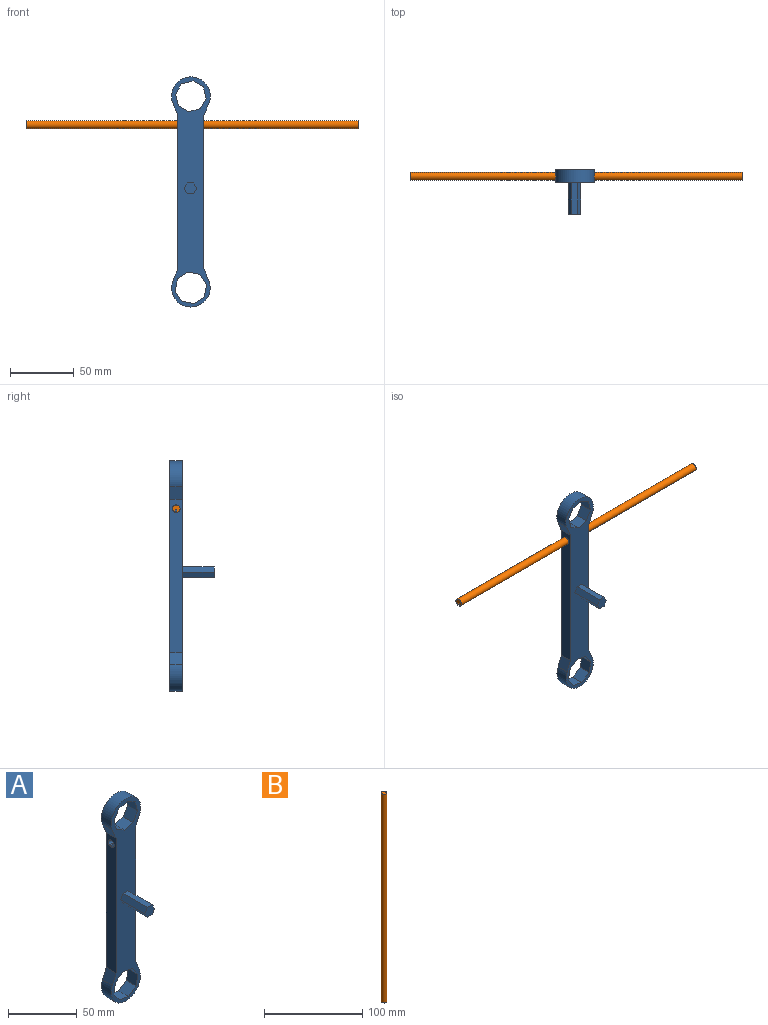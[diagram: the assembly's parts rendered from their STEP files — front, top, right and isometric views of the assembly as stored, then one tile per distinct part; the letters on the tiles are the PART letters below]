
ASSEMBLY  parts=2 mates=1
PART A: 37 faces, bbox 30.4x35x180.3 mm
  f0: plane 120x10mm, normal (1,0,0), area 1174.4mm2, adj f4,f5,f24,f25,f33,f34,f35,f36
  f1: plane 120x10mm, normal (-1,0,0), area 1174.4mm2, adj f2,f7,f24,f25,f33,f34,f35,f36
  f2: plane 10x9.24mm, normal (-0.92,0,0.38), area 100mm2, adj f1,f3,f24,f25
  f3: cylinder r=15.08mm len=30.16mm, axis (0,1,0), area 591.8mm2, adj f2,f4,f24,f25
  f4: plane 10x9.24mm, normal (0.92,0,0.38), area 100mm2, adj f0,f3,f24,f25
  f5: plane 10x10mm, normal (0.92,0,-0.39), area 108.5mm2, adj f0,f6,f24,f25
  f6: cylinder r=15.18mm len=30.36mm, axis (0,1,0), area 578.8mm2, adj f5,f7,f24,f25
  f7: plane 10x10mm, normal (-0.92,0,-0.39), area 108.5mm2, adj f1,f6,f24,f25
  f8: plane 10x8.02mm, normal (-0.51,0,-0.86), area 93mm2, adj f9,f22,f24,f25
  f9: plane 10x9mm, normal (-0.97,0,-0.25), area 93mm2, adj f8,f10,f24,f25
  f10: plane 10x8.02mm, normal (-0.86,0,0.51), area 93mm2, adj f9,f11,f24,f25
  f11: plane 10x9mm, normal (-0.25,0,0.97), area 93mm2, adj f10,f12,f24,f25
  f12: plane 10x8.02mm, normal (0.51,0,0.86), area 93mm2, adj f11,f13,f24,f25
  f13: plane 10x9mm, normal (0.97,0,0.25), area 93mm2, adj f12,f14,f24,f25
  f14: plane 10x8.02mm, normal (0.86,0,-0.51), area 93mm2, adj f13,f22,f24,f25
  f15: plane 10x7.99mm, normal (0.83,0,0.56), area 96.6mm2, adj f16,f23,f24,f25
  f16: plane 10x9.49mm, normal (0.98,0,-0.19), area 96.6mm2, adj f15,f17,f24,f25
  f17: plane 10x7.99mm, normal (0.56,0,-0.83), area 96.6mm2, adj f16,f18,f24,f25
  f18: plane 10x9.49mm, normal (-0.19,0,-0.98), area 96.6mm2, adj f17,f19,f24,f25
  f19: plane 10x7.99mm, normal (-0.83,0,-0.56), area 96.6mm2, adj f18,f20,f24,f25
  f20: plane 10x9.49mm, normal (-0.98,0,0.19), area 96.6mm2, adj f19,f21,f24,f25
  f21: plane 10x7.99mm, normal (-0.56,0,0.83), area 96.6mm2, adj f20,f23,f24,f25
  f22: plane 10x9mm, normal (0.25,0,-0.97), area 93mm2, adj f8,f14,f24,f25
  f23: plane 10x9.49mm, normal (0.19,0,0.98), area 96.6mm2, adj f15,f21,f24,f25
  f24: plane 180.26x30.36mm, normal (0,-1,0), area 2999mm2, adj f0,f1,f2,f3,f4,f5,f6,f7
  f25: plane 180.26x30.36mm, normal (0,1,0), area 3064mm2, adj f0,f1,f2,f3,f4,f5,f6,f7
  f26: plane 25x4.33mm, normal (-0.87,0,-0.5), area 125mm2, adj f24,f27,f31,f32
  f27: plane 25x5mm, normal (0,0,-1), area 125mm2, adj f24,f26,f28,f32
  f28: plane 25x4.33mm, normal (0.87,0,-0.5), area 125mm2, adj f24,f27,f29,f32
  f29: plane 25x4.33mm, normal (0.87,0,0.5), area 125mm2, adj f24,f28,f30,f32
  f30: plane 25x5mm, normal (0,0,1), area 125mm2, adj f24,f29,f31,f32
  f31: plane 25x4.33mm, normal (-0.87,0,0.5), area 125mm2, adj f24,f26,f30,f32
  f32: plane 10x8.66mm, normal (0,-1,0), area 65mm2, adj f26,f27,f28,f29,f30,f31
  f33: plane 20.23x2mm, normal (0,1,0), area 40.5mm2, adj f0,f1,f34,f36
  f34: cylinder r=3mm len=20.23mm, axis (1,0,0), area 354.9mm2, adj f0,f1,f33,f35
  f35: plane 20.23x2mm, normal (0,-1,0), area 40.4mm2, adj f0,f1,f34,f36
  f36: plane 20.23x1.3mm, normal (0,0,1), area 26.3mm2, adj f0,f1,f33,f35
PART B: 6 faces, bbox 5.9x6x260 mm
  f0: plane 260x2mm, normal (0,-1,0), area 520mm2, adj f1,f3,f4,f5
  f1: cylinder r=3mm len=260mm, axis (0,0,-1), area 4560.1mm2, adj f0,f2,f4,f5
  f2: plane 260x2.02mm, normal (0,1,0), area 525.3mm2, adj f1,f3,f4,f5
  f3: plane 260x1.3mm, normal (1,0,0), area 338mm2, adj f0,f2,f4,f5
  f4: plane 6x5.94mm, normal (0,0,1), area 25.6mm2, adj f0,f1,f2,f3
  f5: plane 6x5.94mm, normal (0,0,-1), area 25.6mm2, adj f0,f1,f2,f3
PLACE A t=(-84.46,-32.68,-15.59)mm
PLACE B rot(axis=(0,1,0),90deg) t=(-237.83,-37.82,40.56)mm
MATE slider B.f1 <-> A.f34  axis (-1,0,0) through (-107.83,-37.82,40.56)mm
